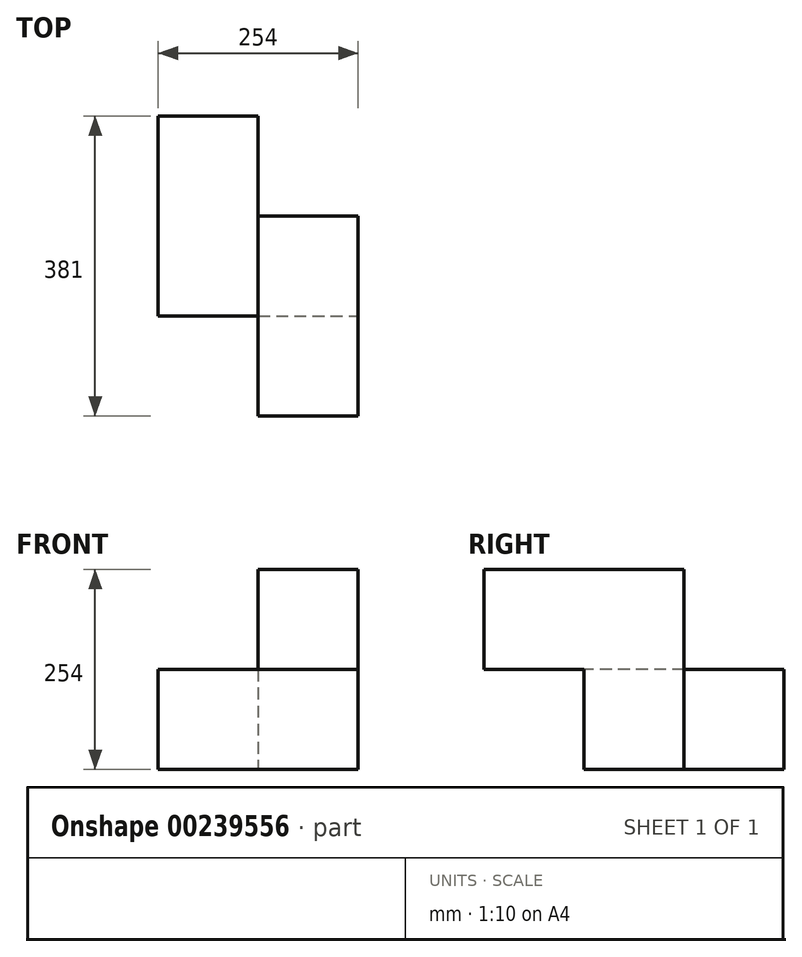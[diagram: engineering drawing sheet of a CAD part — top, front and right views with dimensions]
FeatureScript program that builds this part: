
annotation { "Feature Type Name" : "Feature", "Feature Type Description" : "" }
export const myFeature = defineFeature(function(context is Context, id is Id, definition is map)
    precondition{}
    {
        {
            var Q0;
            Q0=qCreatedBy(makeId("Front.planeOp"),FACE);
            var sketch = newSketch(context, id + "F0", { "sketchPlane" : qUnion([Q0])});
            skLineSegment(sketch, "E0.bottom", {"start": v(63.5, 63.5) * mm, "end": v(-63.5, 63.5) * mm});
            skLineSegment(sketch, "E0.top", {"start": v(63.5, -63.5) * mm, "end": v(-63.5, -63.5) * mm});
            skLineSegment(sketch, "E0.left", {"start": v(63.5, 63.5) * mm, "end": v(63.5, -63.5) * mm});
            skLineSegment(sketch, "E0.right", {"start": v(-63.5, 63.5) * mm, "end": v(-63.5, -63.5) * mm});
            skPoint(sketch, "E0.middle", {"position": v(0, 0) * mm});
            skSolve(sketch);
        }
        {
            var Q0;
            Q0 = qSketchRegion(id + "F0", true);
            extrude(context, id + "F1", {"entities" : qUnion([Q0]), "endBound" : BoundingType.SYMMETRIC, "depth" : 254 * mm});
        }
        {
            var Q0;
            Q0=makeQuery(id+"F1.opExtrude","SWEPT_FACE",FACE,{"disambiguationData":[OSD([sQuery(id+"F0.wireOp",EDGE,"E0.left")])]});
            var sketch = newSketch(context, id + "F2", { "sketchPlane" : qUnion([Q0])});
            skLineSegment(sketch, "E1.bottom", {"start": v(-127, 63.5) * mm, "end": v(0, 63.5) * mm});
            skLineSegment(sketch, "E1.top", {"start": v(-127, -63.5) * mm, "end": v(0, -63.5) * mm});
            skLineSegment(sketch, "E1.left", {"start": v(-127, 63.5) * mm, "end": v(-127, -63.5) * mm});
            skLineSegment(sketch, "E1.right", {"start": v(0, 63.5) * mm, "end": v(0, -63.5) * mm});
            skSolve(sketch);
        }
        {
            var Q0;
            Q0 = qSketchRegion(id + "F2", true);
            extrude(context, id + "F3", {"entities" : qUnion([Q0]), "operationType" : NewBodyOperationType.ADD, "depth" : 127 * mm});
        }
        {
            var Q0;
            Q0=makeQuery(id+"F3.boolean.opBoolean","MERGE",FACE,{"derivedFrom":[makeQuery(id+"F1.opExtrude","SWEPT_FACE",FACE,{"disambiguationData":[OSD([sQuery(id+"F0.wireOp",EDGE,"E0.bottom")])]}),makeQuery(id+"F3.opExtrude","SWEPT_FACE",FACE,{"disambiguationData":[OSD([sQuery(id+"F2.wireOp",EDGE,"E1.bottom")])]})]});
            var sketch = newSketch(context, id + "F4", { "sketchPlane" : qUnion([Q0])});
            skLineSegment(sketch, "E2.bottom", {"start": v(63.5, 0) * mm, "end": v(190.5, 0) * mm});
            skLineSegment(sketch, "E2.top", {"start": v(63.5, -127) * mm, "end": v(190.5, -127) * mm});
            skLineSegment(sketch, "E2.left", {"start": v(63.5, 0) * mm, "end": v(63.5, -127) * mm});
            skLineSegment(sketch, "E2.right", {"start": v(190.5, 0) * mm, "end": v(190.5, -127) * mm});
            skSolve(sketch);
        }
        {
            var Q0;
            Q0 = qSketchRegion(id + "F4", true);
            extrude(context, id + "F5", {"entities" : qUnion([Q0]), "operationType" : NewBodyOperationType.ADD, "depth" : 127 * mm});
        }
        {
            var Q0;
            Q0=makeQuery(id+"F5.boolean.opBoolean","MERGE",FACE,{"derivedFrom":[makeQuery(id+"F3.boolean.opBoolean","MERGE",FACE,{"derivedFrom":[makeQuery(id+"F1.opExtrude","CAP_FACE",FACE,{"disambiguationData":[OSD([sQuery(id+"F0.wireOp",EDGE,"E0.bottom"),sQuery(id+"F0.wireOp",EDGE,"E0.top"),sQuery(id+"F0.wireOp",EDGE,"E0.left"),sQuery(id+"F0.wireOp",EDGE,"E0.right")])],"isStart":false}),makeQuery(id+"F3.opExtrude","SWEPT_FACE",FACE,{"disambiguationData":[OSD([sQuery(id+"F2.wireOp",EDGE,"E1.left")])]})]}),makeQuery(id+"F5.opExtrude","SWEPT_FACE",FACE,{"disambiguationData":[OSD([sQuery(id+"F4.wireOp",EDGE,"E2.top")])]})]});
            var sketch = newSketch(context, id + "F6", { "sketchPlane" : qUnion([Q0])});
            skLineSegment(sketch, "E3.bottom", {"start": v(63.5, 190.5) * mm, "end": v(190.5, 190.5) * mm});
            skLineSegment(sketch, "E3.top", {"start": v(63.5, 63.5) * mm, "end": v(190.5, 63.5) * mm});
            skLineSegment(sketch, "E3.left", {"start": v(63.5, 190.5) * mm, "end": v(63.5, 63.5) * mm});
            skLineSegment(sketch, "E3.right", {"start": v(190.5, 190.5) * mm, "end": v(190.5, 63.5) * mm});
            skSolve(sketch);
        }
        {
            var Q0;
            Q0 = qSketchRegion(id + "F6", true);
            extrude(context, id + "F7", {"entities" : qUnion([Q0]), "operationType" : NewBodyOperationType.ADD, "depth" : 127 * mm});
        }
    });
